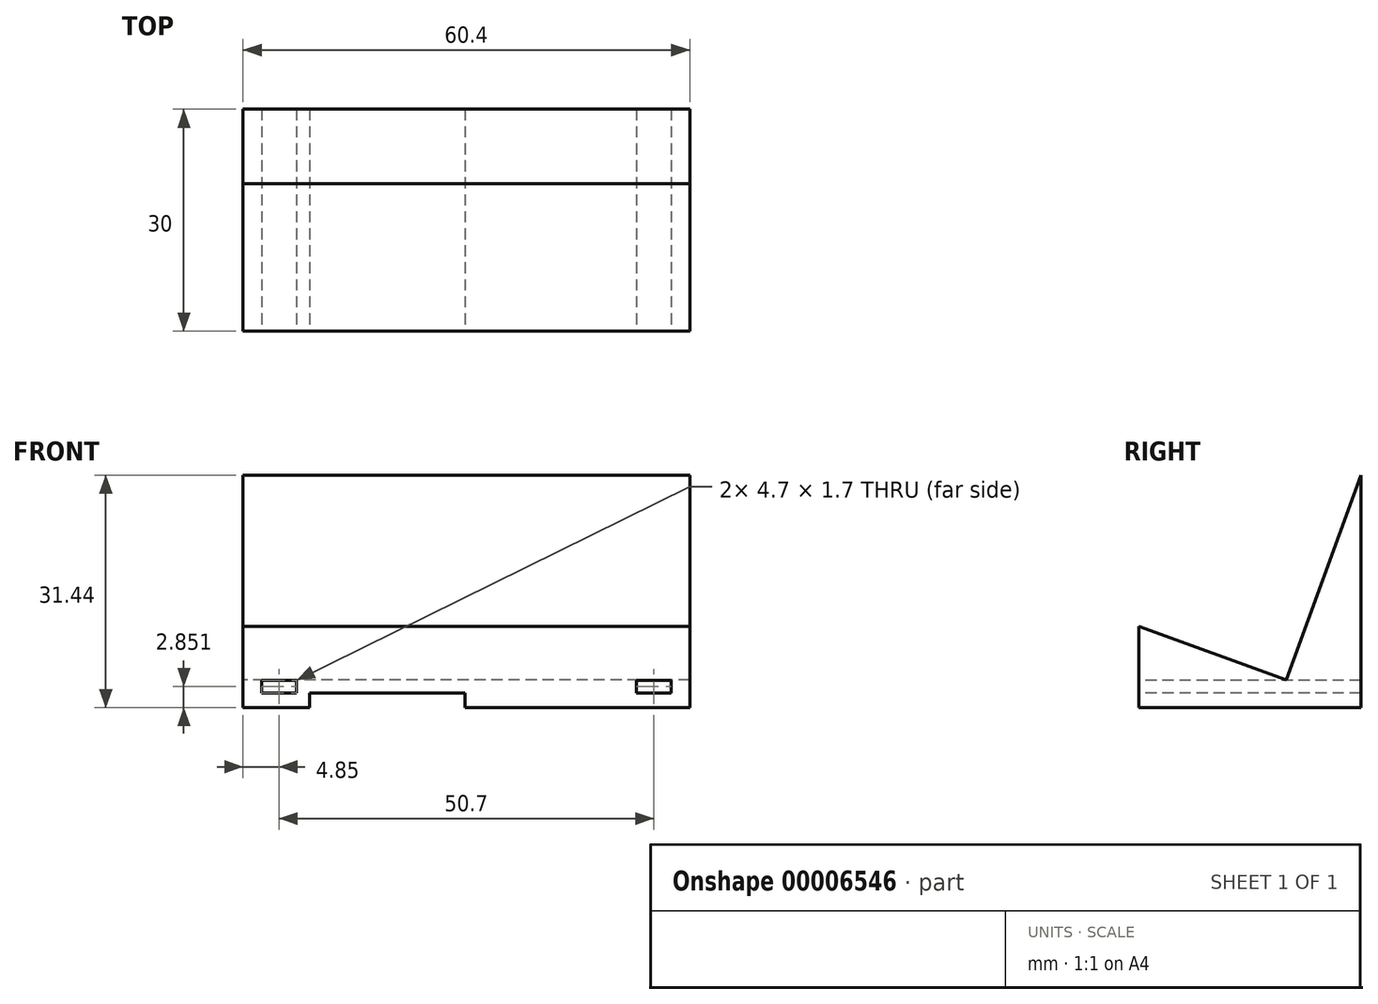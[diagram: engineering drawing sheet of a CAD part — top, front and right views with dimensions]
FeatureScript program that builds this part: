
annotation { "Feature Type Name" : "Feature", "Feature Type Description" : "" }
export const myFeature = defineFeature(function(context is Context, id is Id, definition is map)
    precondition{}
    {
        {
            var Q0;
            Q0=qCreatedBy(makeId("Right.planeOp"),FACE);
            var sketch = newSketch(context, id + "F0", { "sketchPlane" : qUnion([Q0])});
            skLineSegment(sketch, "E0", {"start": v(-0.7, 36.04) * mm, "end": v(-0.7, 67.48) * mm});
            skLineSegment(sketch, "E1", {"start": v(-0.7, 67.48) * mm, "end": v(-10.79, 39.8) * mm});
            skLineSegment(sketch, "E2", {"start": v(-10.79, 39.8) * mm, "end": v(-30.7, 47.04) * mm});
            skLineSegment(sketch, "E3", {"start": v(-30.7, 47.04) * mm, "end": v(-30.7, 36.04) * mm});
            skLineSegment(sketch, "E4", {"start": v(-30.7, 36.04) * mm, "end": v(-0.7, 36.04) * mm});
            skSolve(sketch);
        }
        {
            var Q0;
            Q0 = qSketchRegion(id + "F0", true);
            extrude(context, id + "F1", {"entities" : qUnion([Q0]), "depth" : 60.4 * mm});
        }
        {
            var Q0;
            Q0=makeQuery(id+"F1.opExtrude","SWEPT_FACE",FACE,{"disambiguationData":[OSD([sQuery(id+"F0.wireOp",EDGE,"E3")])]});
            var sketch = newSketch(context, id + "F2", { "sketchPlane" : qUnion([Q0])});
            skLineSegment(sketch, "E5", {"start": v(30, 36.04) * mm, "end": v(30, 38.04) * mm});
            skLineSegment(sketch, "E6", {"start": v(30, 38.04) * mm, "end": v(9, 38.04) * mm});
            skLineSegment(sketch, "E7", {"start": v(9, 38.04) * mm, "end": v(9, 36.04) * mm});
            skLineSegment(sketch, "E8.bottom", {"start": v(2.5, 39.74) * mm, "end": v(7.2, 39.74) * mm});
            skLineSegment(sketch, "E8.top", {"start": v(2.5, 38.04) * mm, "end": v(7.2, 38.04) * mm});
            skLineSegment(sketch, "E8.left", {"start": v(2.5, 39.74) * mm, "end": v(2.5, 38.04) * mm});
            skLineSegment(sketch, "E8.right", {"start": v(7.2, 39.74) * mm, "end": v(7.2, 38.04) * mm});
            skLineSegment(sketch, "E9.bottom", {"start": v(53.2, 39.74) * mm, "end": v(57.9, 39.74) * mm});
            skLineSegment(sketch, "E9.top", {"start": v(53.2, 38.04) * mm, "end": v(57.9, 38.04) * mm});
            skLineSegment(sketch, "E9.left", {"start": v(53.2, 39.74) * mm, "end": v(53.2, 38.04) * mm});
            skLineSegment(sketch, "E9.right", {"start": v(57.9, 39.74) * mm, "end": v(57.9, 38.04) * mm});
            skSolve(sketch);
        }
        {
            var Q0;
            {var subQ2=sQuery(id+"F2.wireOp",EDGE,"E5");Q0=makeQuery(id+"F2.imprint","IMPRINT",FACE,{"disambiguationData":[TD([[makeQuery(id+"F2.imprint","IMPRINT",EDGE,{"derivedFrom":subQ2}),1.0]])]});}
            var Q1;
            Q1=makeQuery(id+"F2.imprint","IMPRINT",FACE,{"disambiguationData":[TD([[makeQuery(id+"F2.imprint","IMPRINT",EDGE,{"derivedFrom":sQuery(id+"F2.wireOp",EDGE,"E9.bottom")}),-1.0]])]});
            var Q2;
            Q2=makeQuery(id+"F2.imprint","IMPRINT",FACE,{"disambiguationData":[TD([[makeQuery(id+"F2.imprint","IMPRINT",EDGE,{"derivedFrom":sQuery(id+"F2.wireOp",EDGE,"E8.bottom")}),-1.0]])]});
            var Q3;
            Q3=makeQuery(id+"F1.opExtrude","SWEPT_FACE",FACE,{"disambiguationData":[OSD([sQuery(id+"F0.wireOp",EDGE,"E0")])]});
            extrude(context, id + "F3", {"entities" : qUnion([Q0, Q1, Q2]), "operationType" : NewBodyOperationType.REMOVE, "endBound" : BoundingType.UP_TO_SURFACE, "oppositeDirection" : true, "endBoundEntityFace" : qUnion([Q3]), "depth" : 25 * mm});
        }
    });
